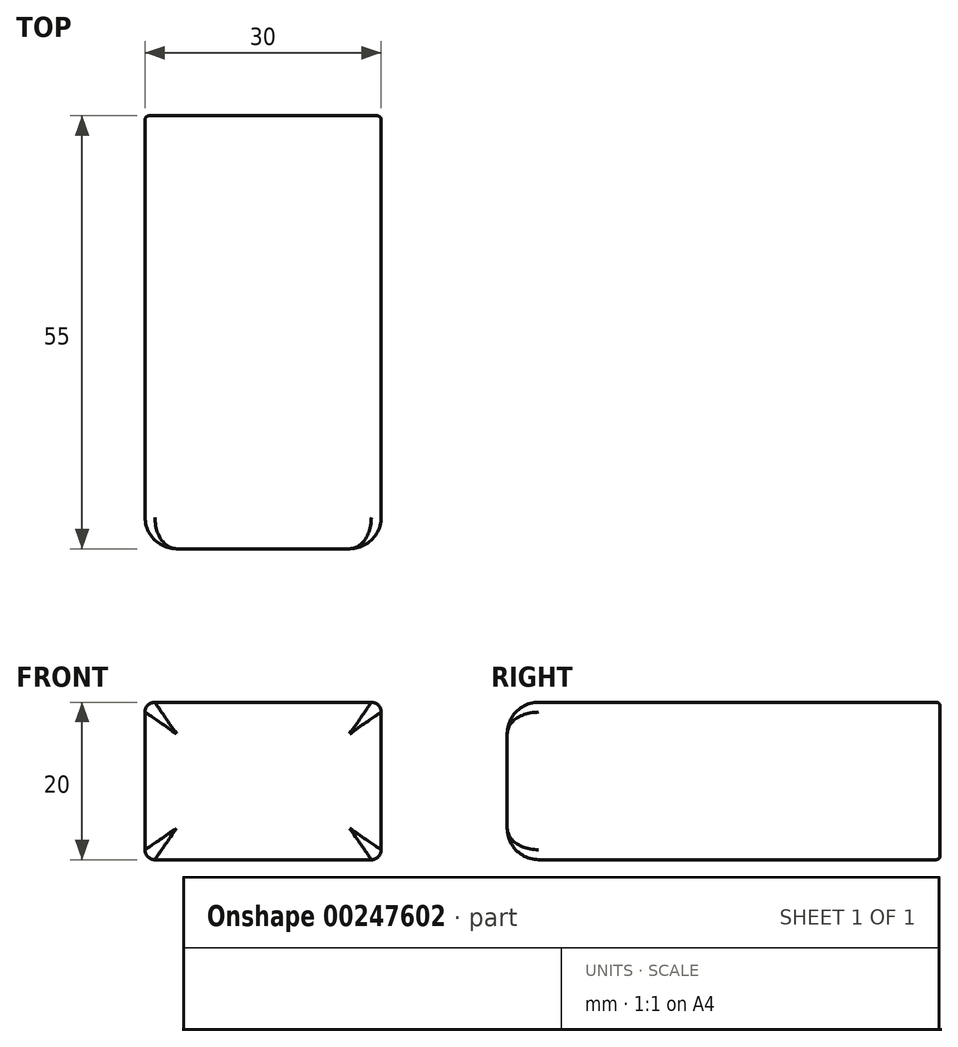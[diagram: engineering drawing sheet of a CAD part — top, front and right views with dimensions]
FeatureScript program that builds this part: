
annotation { "Feature Type Name" : "Feature", "Feature Type Description" : "" }
export const myFeature = defineFeature(function(context is Context, id is Id, definition is map)
    precondition{}
    {
        {
            var Q0;
            Q0=qCreatedBy(makeId("Top.planeOp"),FACE);
            var sketch = newSketch(context, id + "F0", { "sketchPlane" : qUnion([Q0])});
            skLineSegment(sketch, "E0.bottom", {"start": v(15, -27.5) * mm, "end": v(-15, -27.5) * mm});
            skLineSegment(sketch, "E0.top", {"start": v(15, 27.5) * mm, "end": v(-15, 27.5) * mm});
            skLineSegment(sketch, "E0.left", {"start": v(15, -27.5) * mm, "end": v(15, 27.5) * mm});
            skLineSegment(sketch, "E0.right", {"start": v(-15, -27.5) * mm, "end": v(-15, 27.5) * mm});
            skPoint(sketch, "E0.middle", {"position": v(0, 0) * mm});
            skSolve(sketch);
        }
        {
            var Q0;
            Q0=qSketchRegion(id+"F0",true);
            extrude(context, id + "F1", {"entities" : qUnion([Q0]), "depth" : 20 * mm, "symmetric" : true});
        }
        {
            var Q0;
            Q0=makeQuery(id+"F1.opExtrude","SWEPT_EDGE",EDGE,{"disambiguationData":[OSD([sQuery(id+"F0.wireOp",EDGE,"E0.bottom"),sQuery(id+"F0.wireOp",EDGE,"E0.right")])]});
            var Q1;
            Q1=makeQuery(id+"F1.opExtrude","SWEPT_EDGE",EDGE,{"disambiguationData":[OSD([sQuery(id+"F0.wireOp",EDGE,"E0.bottom"),sQuery(id+"F0.wireOp",EDGE,"E0.left")])]});
            var Q2;
            Q2=makeQuery(id+"F1.opExtrude","CAP_EDGE",EDGE,{"disambiguationData":[OSD([sQuery(id+"F0.wireOp",EDGE,"E0.bottom")])],"isStart":false});
            var Q3;
            Q3=makeQuery(id+"F1.opExtrude","CAP_EDGE",EDGE,{"disambiguationData":[OSD([sQuery(id+"F0.wireOp",EDGE,"E0.bottom")])],"isStart":true});
            fillet(context, id + "F2", {"entities" : qUnion([Q0, Q1, Q2, Q3]), "radius" : 4 * mm, "tangentPropagation" : true, "allowEdgeOverflow" : false});
        }
        {
            var Q0;
            Q0=makeQuery(id+"F1.opExtrude","CAP_EDGE",EDGE,{"disambiguationData":[OSD([sQuery(id+"F0.wireOp",EDGE,"E0.left")])],"isStart":false});
            var Q1;
            Q1=makeQuery(id+"F1.opExtrude","CAP_EDGE",EDGE,{"disambiguationData":[OSD([sQuery(id+"F0.wireOp",EDGE,"E0.left")])],"isStart":true});
            var Q2;
            Q2=makeQuery(id+"F1.opExtrude","CAP_EDGE",EDGE,{"disambiguationData":[OSD([sQuery(id+"F0.wireOp",EDGE,"E0.right")])],"isStart":true});
            var Q3;
            Q3=makeQuery(id+"F1.opExtrude","CAP_EDGE",EDGE,{"disambiguationData":[OSD([sQuery(id+"F0.wireOp",EDGE,"E0.right")])],"isStart":false});
            fillet(context, id + "F3", {"entities" : qUnion([Q0, Q1, Q2, Q3]), "radius" : 1.25 * mm, "tangentPropagation" : true, "allowEdgeOverflow" : false});
        }
        {
            var Q0;
            Q0=makeQuery(id+"F1.opExtrude","SWEPT_FACE",FACE,{"disambiguationData":[OSD([sQuery(id+"F0.wireOp",EDGE,"E0.top")])]});
            fillet(context, id + "F4", {"entities" : qUnion([Q0]), "radius" : .5 * mm, "tangentPropagation" : true, "allowEdgeOverflow" : false});
        }
    });
